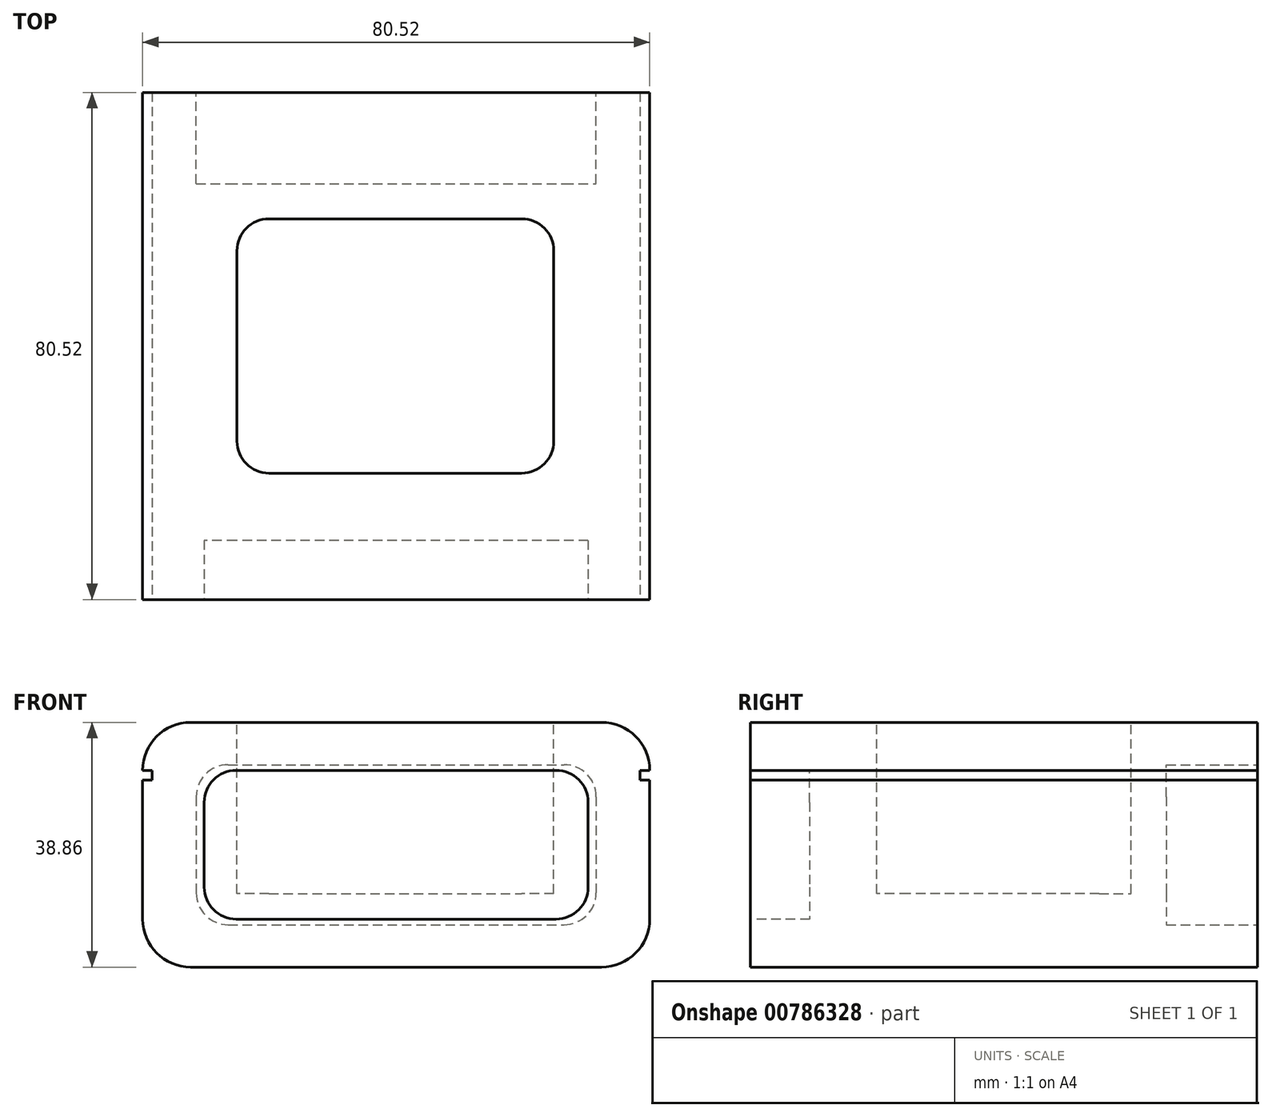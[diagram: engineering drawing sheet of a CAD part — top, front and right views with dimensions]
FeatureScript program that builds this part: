
annotation { "Feature Type Name" : "Feature", "Feature Type Description" : "" }
export const myFeature = defineFeature(function(context is Context, id is Id, definition is map)
    precondition{}
    {
        {
            var Q0;
            Q0=qCreatedBy(makeId("Front.planeOp"),FACE);
            var sketch = newSketch(context, id + "F0", { "sketchPlane" : qUnion([Q0])});
            skLineSegment(sketch, "E0.bottom", {"start": v(32.64, 19.43) * mm, "end": v(-32.64, 19.43) * mm});
            skLineSegment(sketch, "E0.top", {"start": v(32.64, -19.43) * mm, "end": v(-32.64, -19.43) * mm});
            skLineSegment(sketch, "E0.left", {"start": v(40.26, 11.81) * mm, "end": v(40.26, -11.81) * mm});
            skLineSegment(sketch, "E0.right", {"start": v(-40.26, 11.81) * mm, "end": v(-40.26, -11.81) * mm});
            skPoint(sketch, "E0.middle", {"position": v(0, 0) * mm});
            skPoint(sketch, "E1.visualSharp", {"position": v(-40.26, 19.43) * mm});
            skArc(sketch, "E1.filletArc", {"start": v(-32.64, 19.43) * mm, "mid": v(-38.03, 17.2) * mm, "end": v(-40.26, 11.81) * mm});
            skPoint(sketch, "E2.visualSharp", {"position": v(40.26, 19.43) * mm});
            skArc(sketch, "E2.filletArc", {"start": v(40.26, 11.81) * mm, "mid": v(38.03, 17.2) * mm, "end": v(32.64, 19.43) * mm});
            skPoint(sketch, "E3.visualSharp", {"position": v(40.26, -19.43) * mm});
            skArc(sketch, "E3.filletArc", {"start": v(32.64, -19.43) * mm, "mid": v(38.03, -17.2) * mm, "end": v(40.26, -11.81) * mm});
            skPoint(sketch, "E4.visualSharp", {"position": v(-40.26, -19.43) * mm});
            skArc(sketch, "E4.filletArc", {"start": v(-40.26, -11.81) * mm, "mid": v(-38.03, -17.2) * mm, "end": v(-32.64, -19.43) * mm});
            skSolve(sketch);
        }
        {
            var Q0;
            Q0=makeQuery(id+"F0.imprint","IMPRINT",FACE,{"disambiguationData":[TD([[makeQuery(id+"F0.imprint","IMPRINT",EDGE,{"derivedFrom":sQuery(id+"F0.wireOp",EDGE,"E0.bottom")}),1.0]])]});
            extrude(context, id + "F1", {"entities" : qUnion([Q0]), "depth" : 80.52 * mm, "offsetDistance" : 25.4 * mm});
        }
        {
            var Q0;
            Q0=makeQuery(id+"F1.opExtrude","CAP_FACE",FACE,{"disambiguationData":[OSD([sQuery(id+"F0.wireOp",EDGE,"E0.bottom"),sQuery(id+"F0.wireOp",EDGE,"E0.top"),sQuery(id+"F0.wireOp",EDGE,"E0.left"),sQuery(id+"F0.wireOp",EDGE,"E0.right"),sQuery(id+"F0.wireOp",EDGE,"E1.filletArc"),sQuery(id+"F0.wireOp",EDGE,"E2.filletArc"),sQuery(id+"F0.wireOp",EDGE,"E3.filletArc"),sQuery(id+"F0.wireOp",EDGE,"E4.filletArc")])],"isStart":false});
            var sketch = newSketch(context, id + "F2", { "sketchPlane" : qUnion([Q0])});
            skLineSegment(sketch, "E5.bottom", {"start": v(25.4, 11.81) * mm, "end": v(-25.4, 11.81) * mm});
            skLineSegment(sketch, "E5.top", {"start": v(25.4, -11.81) * mm, "end": v(-25.4, -11.81) * mm});
            skLineSegment(sketch, "E5.left", {"start": v(30.48, 6.73) * mm, "end": v(30.48, -6.73) * mm});
            skLineSegment(sketch, "E5.right", {"start": v(-30.48, 6.73) * mm, "end": v(-30.48, -6.73) * mm});
            skPoint(sketch, "E5.middle", {"position": v(0, 0) * mm});
            skPoint(sketch, "E6.visualSharp", {"position": v(-30.48, 11.81) * mm});
            skArc(sketch, "E6.filletArc", {"start": v(-25.4, 11.81) * mm, "mid": v(-29, 10.32) * mm, "end": v(-30.48, 6.73) * mm});
            skPoint(sketch, "E7.visualSharp", {"position": v(30.48, 11.81) * mm});
            skArc(sketch, "E7.filletArc", {"start": v(30.48, 6.73) * mm, "mid": v(29, 10.32) * mm, "end": v(25.4, 11.81) * mm});
            skPoint(sketch, "E8.visualSharp", {"position": v(30.48, -11.81) * mm});
            skArc(sketch, "E8.filletArc", {"start": v(25.4, -11.81) * mm, "mid": v(29, -10.32) * mm, "end": v(30.48, -6.73) * mm});
            skPoint(sketch, "E9.visualSharp", {"position": v(-30.48, -11.81) * mm});
            skArc(sketch, "E9.filletArc", {"start": v(-30.48, -6.73) * mm, "mid": v(-29, -10.32) * mm, "end": v(-25.4, -11.81) * mm});
            skSolve(sketch);
        }
        {
            var Q0;
            Q0=makeQuery(id+"F2.imprint","IMPRINT",FACE,{"disambiguationData":[TD([[makeQuery(id+"F2.imprint","IMPRINT",EDGE,{"derivedFrom":sQuery(id+"F2.wireOp",EDGE,"E5.bottom")}),1.0]])]});
            extrude(context, id + "F3", {"entities" : qUnion([Q0]), "operationType" : NewBodyOperationType.REMOVE, "oppositeDirection" : true, "depth" : 9.4 * mm, "offsetDistance" : 25.4 * mm});
        }
        {
            var Q0;
            Q0=makeQuery(id+"F1.opExtrude","CAP_FACE",FACE,{"disambiguationData":[OSD([sQuery(id+"F0.wireOp",EDGE,"E0.bottom"),sQuery(id+"F0.wireOp",EDGE,"E0.top"),sQuery(id+"F0.wireOp",EDGE,"E0.left"),sQuery(id+"F0.wireOp",EDGE,"E0.right"),sQuery(id+"F0.wireOp",EDGE,"E1.filletArc"),sQuery(id+"F0.wireOp",EDGE,"E2.filletArc"),sQuery(id+"F0.wireOp",EDGE,"E3.filletArc"),sQuery(id+"F0.wireOp",EDGE,"E4.filletArc")])],"isStart":false});
            var sketch = newSketch(context, id + "F4", { "sketchPlane" : qUnion([Q0])});
            skLineSegment(sketch, "E10", {"start": v(40.26, 11.81) * mm, "end": v(38.74, 11.81) * mm});
            skLineSegment(sketch, "E11", {"start": v(38.74, 11.81) * mm, "end": v(38.74, 10.29) * mm});
            skLineSegment(sketch, "E12", {"start": v(38.74, 10.29) * mm, "end": v(40.26, 10.29) * mm});
            skLineSegment(sketch, "E13", {"start": v(40.26, 10.29) * mm, "end": v(40.26, 11.81) * mm});
            skLineSegment(sketch, "E14", {"start": v(-40.26, 11.81) * mm, "end": v(-38.74, 11.81) * mm});
            skLineSegment(sketch, "E15", {"start": v(-38.74, 11.81) * mm, "end": v(-38.74, 10.29) * mm});
            skLineSegment(sketch, "E16", {"start": v(-38.74, 10.29) * mm, "end": v(-40.26, 10.29) * mm});
            skLineSegment(sketch, "E17", {"start": v(-40.26, 10.29) * mm, "end": v(-40.26, 11.81) * mm});
            skSolve(sketch);
        }
        {
            var Q0;
            Q0=makeQuery(id+"F4.imprint","IMPRINT",FACE,{"disambiguationData":[TD([[makeQuery(id+"F4.imprint","IMPRINT",EDGE,{"derivedFrom":sQuery(id+"F4.wireOp",EDGE,"E14")}),-1.0]])]});
            var Q1;
            Q1=makeQuery(id+"F4.imprint","IMPRINT",FACE,{"disambiguationData":[TD([[makeQuery(id+"F4.imprint","IMPRINT",EDGE,{"derivedFrom":sQuery(id+"F4.wireOp",EDGE,"E10")}),1.0]])]});
            extrude(context, id + "F5", {"entities" : qUnion([Q0, Q1]), "operationType" : NewBodyOperationType.REMOVE, "endBound" : BoundingType.THROUGH_ALL, "oppositeDirection" : true, "depth" : 25.4 * mm, "offsetDistance" : 25.4 * mm});
        }
        {
            var Q0;
            Q0=makeQuery(id+"F1.opExtrude","SWEPT_FACE",FACE,{"disambiguationData":[OSD([sQuery(id+"F0.wireOp",EDGE,"E0.bottom")])]});
            var sketch = newSketch(context, id + "F6", { "sketchPlane" : qUnion([Q0])});
            skLineSegment(sketch, "E18.bottom", {"start": v(-20.2, -20.07) * mm, "end": v(19.94, -20.07) * mm});
            skLineSegment(sketch, "E18.top", {"start": v(-20.2, -60.45) * mm, "end": v(19.94, -60.45) * mm});
            skLineSegment(sketch, "E18.left", {"start": v(-25.27, -25.15) * mm, "end": v(-25.27, -55.37) * mm});
            skLineSegment(sketch, "E18.right", {"start": v(25.02, -25.15) * mm, "end": v(25.02, -55.37) * mm});
            skLineSegment(sketch, "E19.0.0", {"start": v(40.26, 0) * mm, "end": v(32.64, 0) * mm});
            skLineSegment(sketch, "E19.0.1", {"start": v(32.64, 0) * mm, "end": v(32.64, -80.52) * mm});
            skLineSegment(sketch, "E19.0.2", {"start": v(32.64, -80.52) * mm, "end": v(40.26, -80.52) * mm});
            skLineSegment(sketch, "E19.0.3", {"start": v(40.26, -80.52) * mm, "end": v(40.26, 0) * mm});
            skPoint(sketch, "E20.visualSharp", {"position": v(-25.27, -20.07) * mm});
            skArc(sketch, "E20.filletArc", {"start": v(-20.2, -20.07) * mm, "mid": v(-23.79, -21.55) * mm, "end": v(-25.27, -25.15) * mm});
            skPoint(sketch, "E21.visualSharp", {"position": v(25.02, -20.07) * mm});
            skArc(sketch, "E21.filletArc", {"start": v(25.02, -25.15) * mm, "mid": v(23.53, -21.55) * mm, "end": v(19.94, -20.07) * mm});
            skPoint(sketch, "E22.visualSharp", {"position": v(25.02, -60.45) * mm});
            skArc(sketch, "E22.filletArc", {"start": v(19.94, -60.45) * mm, "mid": v(23.53, -58.96) * mm, "end": v(25.02, -55.37) * mm});
            skPoint(sketch, "E23.visualSharp", {"position": v(-25.27, -60.45) * mm});
            skArc(sketch, "E23.filletArc", {"start": v(-25.27, -55.37) * mm, "mid": v(-23.79, -58.96) * mm, "end": v(-20.2, -60.45) * mm});
            skSolve(sketch);
        }
        {
            var Q0;
            Q0=makeQuery(id+"F6.imprint","IMPRINT",FACE,{"disambiguationData":[TD([[makeQuery(id+"F6.imprint","IMPRINT",EDGE,{"derivedFrom":sQuery(id+"F6.wireOp",EDGE,"E18.bottom")}),-1.0]])]});
            extrude(context, id + "F7", {"entities" : qUnion([Q0]), "operationType" : NewBodyOperationType.REMOVE, "oppositeDirection" : true, "depth" : 27.18 * mm, "offsetDistance" : 25.4 * mm});
        }
        {
            var Q0;
            Q0=makeQuery(id+"F1.opExtrude","CAP_FACE",FACE,{"disambiguationData":[OSD([sQuery(id+"F0.wireOp",EDGE,"E0.bottom"),sQuery(id+"F0.wireOp",EDGE,"E0.top"),sQuery(id+"F0.wireOp",EDGE,"E0.left"),sQuery(id+"F0.wireOp",EDGE,"E0.right"),sQuery(id+"F0.wireOp",EDGE,"E1.filletArc"),sQuery(id+"F0.wireOp",EDGE,"E2.filletArc"),sQuery(id+"F0.wireOp",EDGE,"E3.filletArc"),sQuery(id+"F0.wireOp",EDGE,"E4.filletArc")])],"isStart":true});
            var sketch = newSketch(context, id + "F8", { "sketchPlane" : qUnion([Q0])});
            skLineSegment(sketch, "E24.bottom", {"start": v(26.67, 12.7) * mm, "end": v(-26.67, 12.7) * mm});
            skLineSegment(sketch, "E24.top", {"start": v(26.67, -12.7) * mm, "end": v(-26.67, -12.7) * mm});
            skLineSegment(sketch, "E24.left", {"start": v(31.75, 7.62) * mm, "end": v(31.75, -7.62) * mm});
            skLineSegment(sketch, "E24.right", {"start": v(-31.75, 7.62) * mm, "end": v(-31.75, -7.62) * mm});
            skPoint(sketch, "E24.middle", {"position": v(0, 0) * mm});
            skPoint(sketch, "E25.visualSharp", {"position": v(-31.75, 12.7) * mm});
            skArc(sketch, "E25.filletArc", {"start": v(-26.67, 12.7) * mm, "mid": v(-30.26, 11.21) * mm, "end": v(-31.75, 7.62) * mm});
            skPoint(sketch, "E26.visualSharp", {"position": v(31.75, 12.7) * mm});
            skArc(sketch, "E26.filletArc", {"start": v(31.75, 7.62) * mm, "mid": v(30.26, 11.21) * mm, "end": v(26.67, 12.7) * mm});
            skPoint(sketch, "E27.visualSharp", {"position": v(31.75, -12.7) * mm});
            skArc(sketch, "E27.filletArc", {"start": v(26.67, -12.7) * mm, "mid": v(30.26, -11.21) * mm, "end": v(31.75, -7.62) * mm});
            skPoint(sketch, "E28.visualSharp", {"position": v(-31.75, -12.7) * mm});
            skArc(sketch, "E28.filletArc", {"start": v(-31.75, -7.62) * mm, "mid": v(-30.26, -11.21) * mm, "end": v(-26.67, -12.7) * mm});
            skSolve(sketch);
        }
        {
            var Q0;
            Q0=makeQuery(id+"F8.imprint","IMPRINT",FACE,{"disambiguationData":[TD([[makeQuery(id+"F8.imprint","IMPRINT",EDGE,{"derivedFrom":sQuery(id+"F8.wireOp",EDGE,"E24.bottom")}),1.0]])]});
            extrude(context, id + "F9", {"entities" : qUnion([Q0]), "operationType" : NewBodyOperationType.REMOVE, "oppositeDirection" : true, "depth" : 14.48 * mm, "offsetDistance" : 25.4 * mm});
        }
    });
